# Revit family: Sanitary_Accessories_Svedholm_One-More-Minute
name_source: partatom
category: Furniture
revit_build: Autodesk Revit 2018 (Build: 20190510_1515(x64)
units: mm (PartAtom-declared; Revit-internal decimal feet)

## family parameters
Cut with Voids When Loaded = No
Host = Face
OmniClass Number = 23.21.11.00
OmniClass Title = Commercial Furniture
Room Calculation Point = No
Shared = No

## types (1)
- ART - (411.600.001)
    BIMobject category = Accessories
    Default Elevation = 1219 mm
    Description = A five minutes hourglass with powder coated stainless steel holder.
    Design country = Sweden
    Edition number = 1
    IFC Classification = Object
    Manufacturer = Svedholm
    Manufacturer country = Sweden
    Manufacturer name = Svedholm
    Material main = Stainless steel
    Material secondary = Glass
    Model = One More Minute
    OmniClass Code = 23-21 11 00
    OmniClass Description = Commercial Furniture
    Product Guid = 26f3b451-67e5-4ba0-8e1b-6d9754e8579f
    Product SKU = One-More-Minute
    Product data url = https://bimobject.com
    Product family = One More Minute
    Product group = Accessories
    Product name = One More Minute
    Product url = https://www.svedholm.se
    QR code = https://bimobject.com
    Secondary material = Svedholm - Glass - Transparent
    URL = https://www.svedholm.se
    Uniclass 2015 Code = Zz_30_60
    Uniclass 2015 Name = Objects

## geometry (parser evidence)
native form markers: Sweep x2
no freeform markers — native parametric forms only
